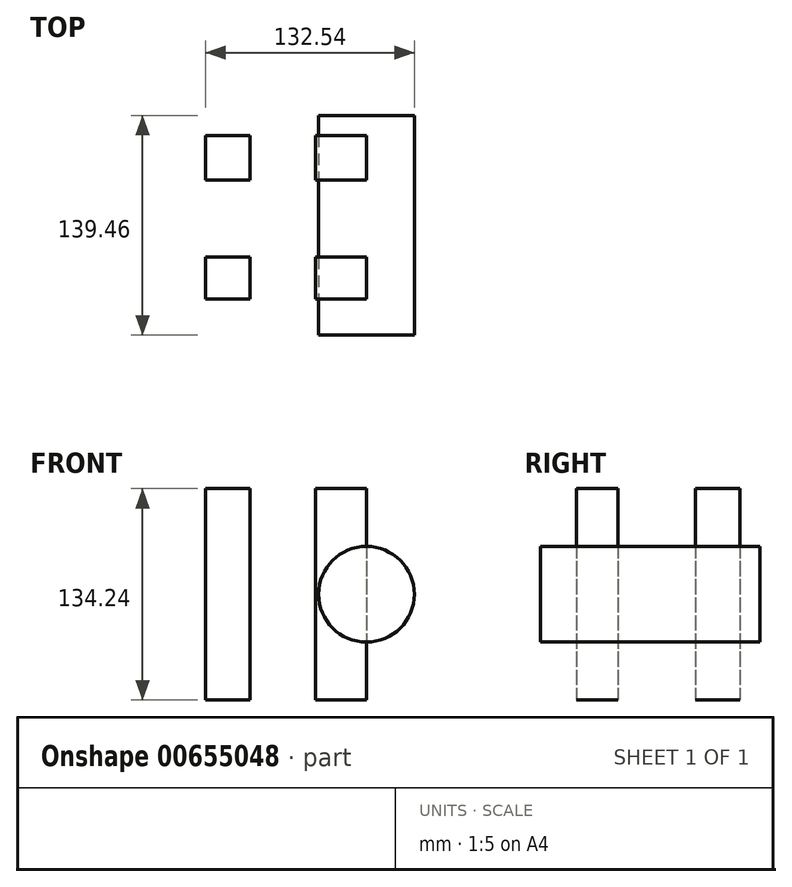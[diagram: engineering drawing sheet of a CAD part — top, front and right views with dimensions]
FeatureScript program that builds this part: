
annotation { "Feature Type Name" : "Feature", "Feature Type Description" : "" }
export const myFeature = defineFeature(function(context is Context, id is Id, definition is map)
    precondition{}
    {
        {
            var Q0;
            Q0=qCreatedBy(makeId("Top.planeOp"),FACE);
            var sketch = newSketch(context, id + "F0", { "sketchPlane" : qUnion([Q0])});
            skLineSegment(sketch, "E0.bottom", {"start": v(55.1, -53.73) * mm, "end": v(-47.05, -53.73) * mm, "construction": true});
            skLineSegment(sketch, "E0.top", {"start": v(55.1, 50.1) * mm, "end": v(-47.05, 50.1) * mm, "construction": true});
            skLineSegment(sketch, "E0.left", {"start": v(55.1, -53.73) * mm, "end": v(55.1, 50.1) * mm, "construction": true});
            skLineSegment(sketch, "E0.right", {"start": v(-47.05, -53.73) * mm, "end": v(-47.05, 50.1) * mm, "construction": true});
            skLineSegment(sketch, "E1", {"start": v(-18.78, 50.1) * mm, "end": v(-18.78, -53.73) * mm, "construction": true});
            skLineSegment(sketch, "E2", {"start": v(22.73, 50.1) * mm, "end": v(22.73, -53.73) * mm, "construction": true});
            skLineSegment(sketch, "E3", {"start": v(-47.05, -27.3) * mm, "end": v(55.1, -27.3) * mm, "construction": true});
            skLineSegment(sketch, "E4", {"start": v(-47.05, 21.88) * mm, "end": v(55.1, 21.88) * mm, "construction": true});
            skLineSegment(sketch, "E5.bottom", {"start": v(-47.05, 50.1) * mm, "end": v(-18.78, 50.1) * mm});
            skLineSegment(sketch, "E5.top", {"start": v(-47.05, 21.88) * mm, "end": v(-18.78, 21.88) * mm});
            skLineSegment(sketch, "E5.left", {"start": v(-47.05, 50.1) * mm, "end": v(-47.05, 21.88) * mm});
            skLineSegment(sketch, "E5.right", {"start": v(-18.78, 50.1) * mm, "end": v(-18.78, 21.88) * mm});
            skLineSegment(sketch, "E6.bottom", {"start": v(55.1, 50.1) * mm, "end": v(22.73, 50.1) * mm});
            skLineSegment(sketch, "E6.top", {"start": v(55.1, 21.88) * mm, "end": v(22.73, 21.88) * mm});
            skLineSegment(sketch, "E6.left", {"start": v(55.1, 50.1) * mm, "end": v(55.1, 21.88) * mm});
            skLineSegment(sketch, "E6.right", {"start": v(22.73, 50.1) * mm, "end": v(22.73, 21.88) * mm});
            skLineSegment(sketch, "E7.bottom", {"start": v(55.1, -53.73) * mm, "end": v(22.73, -53.73) * mm});
            skLineSegment(sketch, "E7.top", {"start": v(55.1, -27.3) * mm, "end": v(22.73, -27.3) * mm});
            skLineSegment(sketch, "E7.left", {"start": v(55.1, -53.73) * mm, "end": v(55.1, -27.3) * mm});
            skLineSegment(sketch, "E7.right", {"start": v(22.73, -53.73) * mm, "end": v(22.73, -27.3) * mm});
            skLineSegment(sketch, "E8.bottom", {"start": v(-47.05, -53.73) * mm, "end": v(-18.78, -53.73) * mm});
            skLineSegment(sketch, "E8.top", {"start": v(-47.05, -27.3) * mm, "end": v(-18.78, -27.3) * mm});
            skLineSegment(sketch, "E8.left", {"start": v(-47.05, -53.73) * mm, "end": v(-47.05, -27.3) * mm});
            skLineSegment(sketch, "E8.right", {"start": v(-18.78, -53.73) * mm, "end": v(-18.78, -27.3) * mm});
            skSolve(sketch);
        }
        {
            var Q0;
            Q0 = qSketchRegion(id + "F0", true);
            extrude(context, id + "F1", {"entities" : qUnion([Q0]), "depth" : 134.24 * mm, "offsetDistance" : 25.4 * mm});
        }
        {
            var Q0;
            Q0=qCreatedBy(makeId("Front.planeOp"),FACE);
            var sketch = newSketch(context, id + "F2", { "sketchPlane" : qUnion([Q0])});
            skLineSegment(sketch, "E9.0", {"start": v(55.1, 134.24) * mm, "end": v(55.1, 0) * mm});
            skCircle(sketch, "E10", {"center": v(55.1, 67.12) * mm, "radius": 30.39 * mm});
            skSolve(sketch);
        }
        {
            var Q0;
            Q0 = qSketchRegion(id + "F2", true);
            var Q1;
            {var subQ0=sQuery(id+"F2.wireOp",EDGE,"E10");var subQ1=sQuery(id+"F2.wireOp",EDGE,"E9.0");var subQ2=makeQuery(id+"F2.imprint","INTERSECT",VERTEX,{"disambiguationData":[OD(0.0)],"derivedFrom":[subQ1,subQ0]});Q1=makeQuery(id+"F2.imprint","IMPRINT",FACE,{"disambiguationData":[TD([[makeQuery(id+"F2.imprint","IMPRINT",EDGE,{"disambiguationData":[TD([[subQ2,1.0]])],"derivedFrom":subQ1}),1.0]])]});}
            extrude(context, id + "F3", {"entities" : qUnion([Q0, Q1]), "oppositeDirection" : true, "depth" : 62.7 * mm, "offsetDistance" : 25.4 * mm, "hasSecondDirection" : true, "secondDirectionOppositeDirection" : false, "secondDirectionDepth" : 76.75 * mm});
        }
    });
